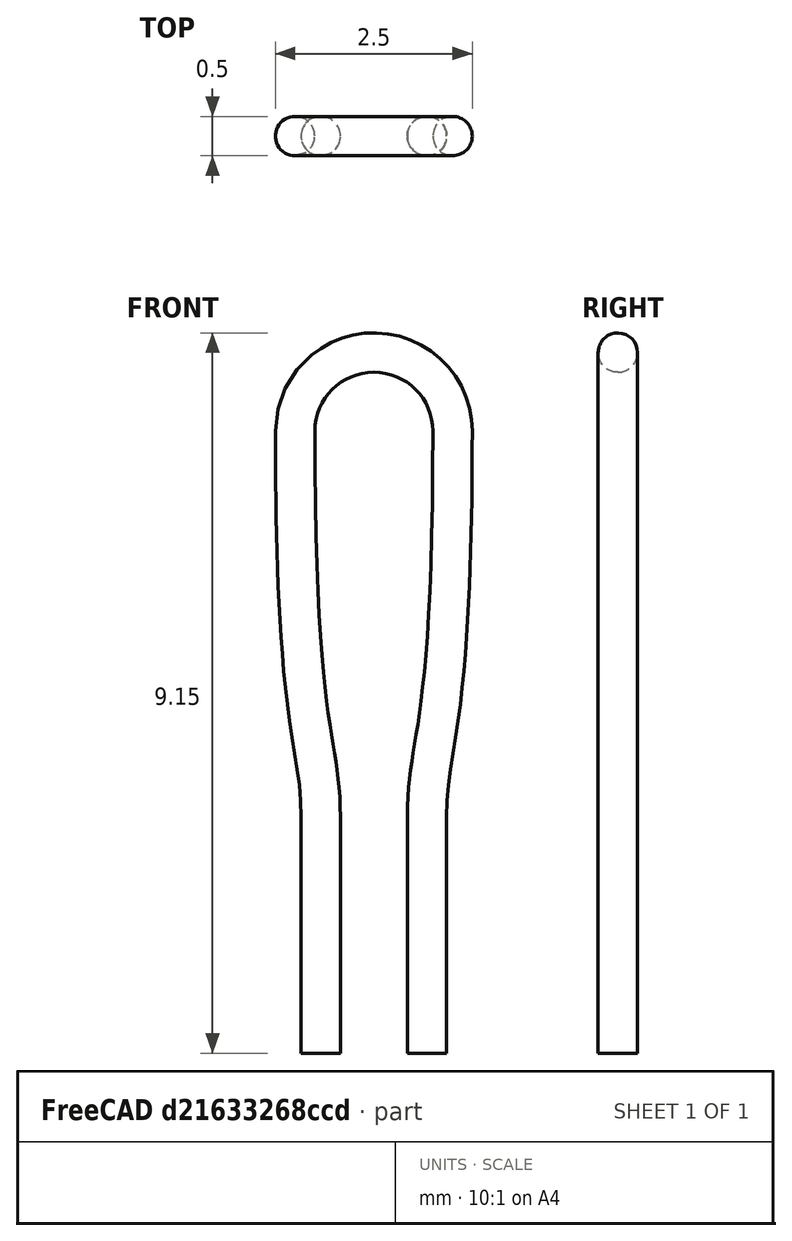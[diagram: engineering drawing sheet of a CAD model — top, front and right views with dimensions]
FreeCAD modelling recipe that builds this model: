
FCSTD DOCUMENT  (FreeCAD 0.17R12018 (Git))
Label: Test_Point_Loop_D2.50mm_Drill1.85mm
License: All rights reserved
LicenseURL: http://en.wikipedia.org/wiki/All_rights_reserved
objects: Sketcher::SketchObject×2, Spreadsheet::Sheet×1, PartDesign::AdditivePipe×1, PartDesign::Body×1, App::Part×1
note: 5 computed .brp shape members not serialized (recipe doc carries the construction recipe); baked Part::Feature solids carry a one-line shape summary decoded from their .brp

FEATURE [Spreadsheet::Sheet] Spreadsheet  label="dims"
  cells = A1="DWire"; B1(DWire)=0.5; A2="DLoop"; B2(DLoop)=2.5; A3="Spacer"; B3(Spacer)=0; A4="DSpacer"; B4(DSpacer)=3; A5="Lall"; B5(Lall)=8.9000000000000004; A6="Ddrill"; B6(Ddrill)=1.8500000000000001; A7="Lbottom"; B7(Lbottom)=3
FEATURE [Sketcher::SketchObject] Sketch001
  MapMode = 5
  Placement = pos=(0,0,0) rot=(1,0,0;1.5708rad)
  expr: Constraints[63] = (dims.DLoop - dims.DWire) / 2
  expr: Constraints[28] = dims.Lall - (dims.DLoop - dims.DWire) / 2
  expr: Constraints[27] = (dims.DLoop - dims.DWire) / 2
  expr: Constraints[30] = dims.Lbottom
  expr: Constraints[32] = dims.Spacer
  expr: Constraints[33] = dims.Ddrill - dims.DWire
  expr: Constraints[34] = (dims.Ddrill - dims.DWire) / 2
  sketch-geometry (25):
    g0: LineSegment StartX=-0.675003 StartY=-3 StartZ=0 EndX=-0.675003 EndY=8.02e-10 EndZ=0
    g1: LineSegment StartX=0.674993 StartY=1.671e-09 StartZ=0 EndX=0.674993 EndY=-3 EndZ=0
    g2: ArcOfCircle CenterX=0 CenterY=4.9 CenterZ=0 NormalX=0 NormalY=0 NormalZ=1 Radius=1 StartAngle=0 EndAngle=3.14159
    g3: LineSegment [constr] StartX=-1 StartY=4.9 StartZ=0 EndX=1 EndY=4.9 EndZ=0
    g4: LineSegment [constr] StartX=-1 StartY=1.543e-09 StartZ=0 EndX=1 EndY=1.543e-09 EndZ=0
    g5: LineSegment [constr] StartX=1 StartY=4.9 StartZ=0 EndX=1 EndY=1.543e-09 EndZ=0
    g6: LineSegment [constr] StartX=-1 StartY=1.543e-09 StartZ=0 EndX=-1 EndY=4.9 EndZ=0
    g7: LineSegment [constr] StartX=-0.675003 StartY=8.02e-10 StartZ=0 EndX=-0.675003 EndY=1 EndZ=0
    g8: LineSegment [constr] StartX=0.674993 StartY=1.671e-09 StartZ=0 EndX=0.674993 EndY=1 EndZ=0
    g9: LineSegment [constr] StartX=-1 StartY=1 StartZ=0 EndX=1 EndY=1 EndZ=0
    g10: LineSegment [constr] StartX=0.674993 StartY=1 StartZ=0 EndX=0.674993 EndY=4.9 EndZ=0
    g11-g14: Circle [constr] x4 (B-spline internal-alignment scaffolding for g15; pole/knot coordinates omitted)
    g15: BSplineCurve PolesCount=4 KnotsCount=2 Degree=3 IsPeriodic=0
    g16: GeomPoint [constr] X=-0.675003 Y=8.02e-10 Z=0
    g17: GeomPoint [constr] X=-1 Y=4.9 Z=0
    g18-g21: Circle [constr] x4 (B-spline internal-alignment scaffolding for g22; pole/knot coordinates omitted)
    g22: BSplineCurve PolesCount=4 KnotsCount=2 Degree=3 IsPeriodic=0
    g23: GeomPoint [constr] X=0.674993 Y=1.671e-09 Z=0
    g24: GeomPoint [constr] X=1 Y=4.9 Z=0
  constraints (58):
    c: Vertical(g0)
    c: Vertical(g1)
    c: Coincident(g3,g2)
    c: Horizontal(g3)
    c: PointOnObject(g2,g3)
    c: Coincident(g3,g2)
    c: PointOnObject(g2,g-2)
    c: Horizontal(g4)
    c: Coincident(g5,g2)
    c: Coincident(g5,g4)
    c: Coincident(g6,g4)
    c: Coincident(g6,g2)
    c: PointOnObject(g0,g4)
    c: PointOnObject(g1,g4)
    c: Vertical(g6)
    c: Vertical(g5)
    c: Coincident(g7,g0)
    c: Vertical(g7)
    c: Coincident(g8,g1)
    c: Vertical(g8)
    c: PointOnObject(g9,g6)
    c: PointOnObject(g9,g5)
    c: Horizontal(g9)
    c: PointOnObject(g7,g9)
    c: PointOnObject(g8,g9)
    c: PointOnObject(g10,g3)
    c: Vertical(g10)
    c: Radius(g2) = 1
    c: DistanceY(g1,g2) = 7.9
    c: DistanceY(g1,g0) = 0
    c: DistanceY(g0,g-1) = 3
    c: Coincident(g10,g8)
    c: DistanceY(g-1,g0) = 0
    c: DistanceX(g0,g1) = 1.35
    c: DistanceX(g0,g-1) = 0.675
    c: Coincident(g11,g0)
    c: Radius(g11) = 0
    c: Equal(g11,g12)
    c: Coincident(g12,g7)
    c: Equal(g11,g13)
    c: Coincident(g13,g9)
    c: Equal(g11,g14)
    c: Coincident(g14,g2)
    c: InternalAlignment(g11-g14 -> g15) x4
    c: InternalAlignment(g16,g15)
    c: InternalAlignment(g17,g15)
    c: Coincident(g18,g1)
    c: Radius(g18) = 0
    c: Equal(g18,g19)
    c: Coincident(g19,g8)
    c: Equal(g18,g20)
    c: Coincident(g20,g9)
    c: Equal(g18,g21)
    c: Coincident(g21,g2)
    c: InternalAlignment(g18-g21 -> g22) x4
    c: InternalAlignment(g23,g22)
    c: InternalAlignment(g24,g22)
    c: DistanceY(g4,g9) = 1
FEATURE [Sketcher::SketchObject] Sketch
  MapMode = 5
  Placement = pos=(0,0,-3) rot=(0,0,1;0rad)
  expr: Constraints[2] = (dims.Ddrill - dims.DWire) / 2
  expr: Constraints[1] = dims.DWire / 2
  sketch-geometry (1):
    g0: Circle CenterX=-0.675 CenterY=0 CenterZ=0 NormalX=0 NormalY=0 NormalZ=1 Radius=0.25
  constraints (3):
    c: PointOnObject(g0,g-1)
    c: Radius(g0) = 0.25
    c: DistanceX(g0,g-1) = 0.675
FEATURE [PartDesign::AdditivePipe] AdditivePipe
  AuxilleryCurvelinear = true
  AuxillerySpineTangent = false
  Binormal = (0,0,0)
  Mode = 0
  Placement = pos=(0,0,-3) rot=(0,0,1;0rad)
  Profile = -> Sketch
  Spine = -> Sketch001 [Edge1,Edge2,Edge3,Edge4,Edge5]
  SpineTangent = false
  Transformation = 0
  Transition = 0
FEATURE [PartDesign::Body] Body  label="Test_Point_Loop_D2.50mm_Drill1.85mm"
  Group = -> [Sketch,Sketch001,AdditivePipe]
  Origin = -> Origin002
  Tip = -> AdditivePipe
FEATURE [App::Part] Part  label="group"
  Group = -> [Body]
  License = CC BY 3.0
  LicenseURL = http://creativecommons.org/licenses/by/3.0/
  Origin = -> Origin
